# Revit family: ---------Plumbing-Valves-Sloan-WES-115
name_source: partatom
category: Plumbing Fixtures
units: mm (PartAtom-declared; Revit-internal decimal feet)

## family parameters
Cut with Voids When Loaded = No
Host = Face
OmniClass Number = 23.45.05.14.99
OmniClass Title = Other Sanitary Washing Plumbing Fixtures
Part Type = Normal
Room Calculation Point = No
Round Connector Dimension = Use Diameter
Shared = No

## types (7) — shared parameters
Assembly Code = D2020300
CW Connection = Yes
Centerline of Supply from Top of Fixture = 24"
Centerline of Supply to Centerline of Valve = 4 3/4"
Default Elevation = 0"
Edition number = 1
Flush Rate = 1.6/1.1 gpf (6.0/4.2 Lpf)
HW Connection = No
Height = 26 1/2"
Keynote = 15410
Manufacturer = Sloan Valve
Operating Water Pressure = 15 – 80 PSI (103 – 552 kPa)
Product Material = Sloan Valve - Finish - Polished Chrome
Product data url = https://www.bimobject.com
URL = www.sloanvalve.com
Valve Pressure Drop = 0.00 psi
Vent Connection = No
Waste Connection = No
Water Inlet Connection Diameter = 1"
zero-valued in all types: CWFU, HWFU, WFU

## per-type parameters (varying)
| type | Description | Part Number |
| WES 115-1.6/1.1 | 1.6/1.1 gpf, Polished Chrome Finish, Fixture Connection Top Spud, Single Flush, UPPERCUT® Exposed Manual Water Closet Flushometer. | 3720300 |
| WES 115-1.6/1.1-U-WWT | 1.6/1.1 gpf, Polished Chrome Finish, 1.25" Flush Connection, Fixture Connection Top Spud, Single Flush, Whitworth Thread, UPPERCUT® Exposed Manual Water Closet Flushometer. | 3720316 |
| WES 115-1.6/1.1-YI | 1.6/1.1 gpf, Double Wall Bumper, Polished Chrome Finish, Fixture Connection Top Spud, Single Flush, UPPERCUT® Exposed Manual Water Closet Flushometer. | 3720306 |
| WES 115-1.6/1.1-T-2-OFST | 1.6/1.1 gpf, Polished Chrome Finish, 1.5" Flush Connection, Fixture Connection Top Spud, Single Flush, 2 Offset, UPPERCUT® Exposed Manual Water Closet Flushometer | 3720304 |
| WES 115-1.6/1.1-1-1/2-OFST-YK | 1.6/1.1 gpf, Polished Chrome Finish, Fixture Connection Top Spud, Single Flush, 1.5 Offset, Solid Ring Pipe Support, UPPERCUT® Exposed Manual Water Closet Flushometer. | 3720301 |
| WES 115-1.6/1.1-WWT | 1.6/1.1 gpf, Polished Chrome Finish, Fixture Connection Top Spud, Single Flush, Whitworth Thread, UPPERCUT® Exposed Manual Water Closet Flushometer | 3720315 |
| WES 115-1.6/1.1-2-OFST | 1.6/1.1 gpf, Polished Chrome Finish, Fixture Connection Top Spud, Single Flush, 2 Offset, UPPERCUT® Exposed Manual Water Closet Flushometer. | 3720303 |

note: column(s) folded — value = type name in every type: Model

## geometry (parser evidence)
native form markers: Sweep x8
no freeform markers — native parametric forms only
